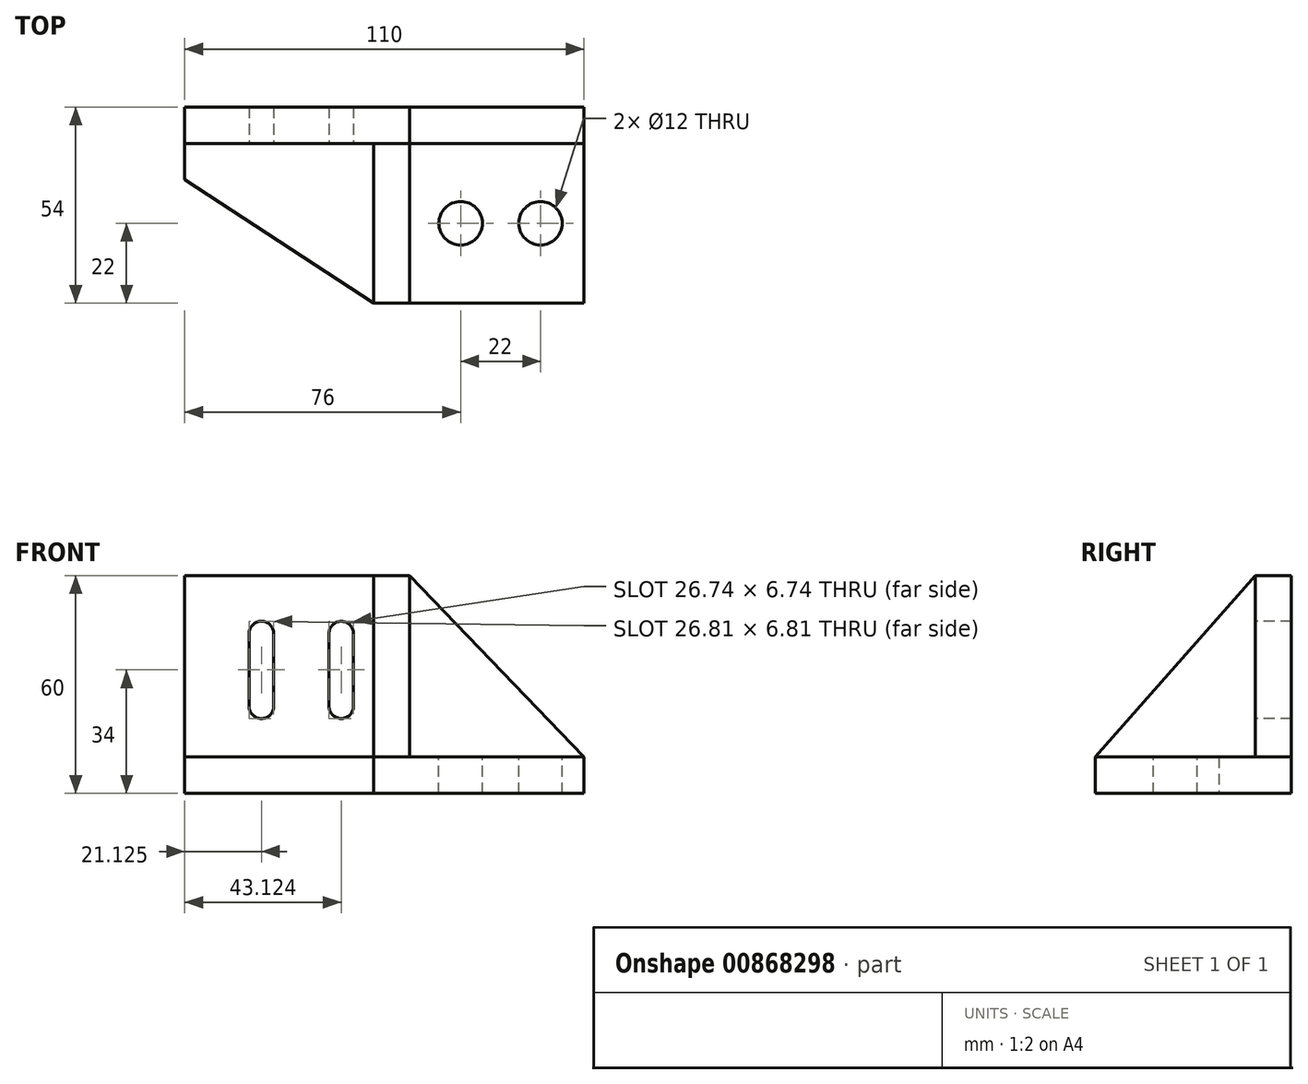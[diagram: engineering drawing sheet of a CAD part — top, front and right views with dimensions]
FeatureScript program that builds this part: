
annotation { "Feature Type Name" : "Feature", "Feature Type Description" : "" }
export const myFeature = defineFeature(function(context is Context, id is Id, definition is map)
    precondition{}
    {
        {
            var Q0;
            Q0=qCreatedBy(makeId("Top.planeOp"),FACE);
            var sketch = newSketch(context, id + "F0", { "sketchPlane" : qUnion([Q0])});
            skLineSegment(sketch, "E0.bottom", {"start": v(29, 27) * mm, "end": v(-29, 27) * mm});
            skLineSegment(sketch, "E0.top", {"start": v(29, -27) * mm, "end": v(-29, -27) * mm});
            skLineSegment(sketch, "E0.left", {"start": v(29, 27) * mm, "end": v(29, -27) * mm});
            skLineSegment(sketch, "E0.right", {"start": v(-29, 27) * mm, "end": v(-29, -27) * mm});
            skPoint(sketch, "E0.middle", {"position": v(0, 0) * mm});
            skLineSegment(sketch, "E1", {"start": v(-29, 27) * mm, "end": v(-81, 27) * mm});
            skLineSegment(sketch, "E2", {"start": v(-81, 27) * mm, "end": v(-81, 7) * mm});
            skLineSegment(sketch, "E3", {"start": v(-29, -27) * mm, "end": v(-81, 7) * mm});
            skSolve(sketch);
        }
        {
            var Q0;
            Q0=makeQuery(id+"F0.imprint","IMPRINT",FACE,{"disambiguationData":[TD([[makeQuery(id+"F0.imprint","IMPRINT",EDGE,{"derivedFrom":sQuery(id+"F0.wireOp",EDGE,"E0.bottom")}),1.0]])]});
            var Q1;
            Q1=makeQuery(id+"F0.imprint","IMPRINT",FACE,{"disambiguationData":[TD([[makeQuery(id+"F0.imprint","IMPRINT",EDGE,{"derivedFrom":sQuery(id+"F0.wireOp",EDGE,"E0.right")}),-1.0]])]});
            extrude(context, id + "F1", {"entities" : qUnion([Q0, Q1]), "depth" : 10 * mm, "offsetDistance" : 25 * mm});
        }
        {
            var Q0;
            Q0=makeQuery(id+"F1.opExtrude","SWEPT_FACE",FACE,{"disambiguationData":[OSD([sQuery(id+"F0.wireOp",EDGE,"E0.bottom")])]});
            var sketch = newSketch(context, id + "F2", { "sketchPlane" : qUnion([Q0])});
            skLineSegment(sketch, "E4", {"start": v(-29, 10) * mm, "end": v(19, 10) * mm});
            skLineSegment(sketch, "E5", {"start": v(19, 10) * mm, "end": v(19, 60) * mm});
            skLineSegment(sketch, "E6", {"start": v(19, 60) * mm, "end": v(-29, 10) * mm});
            skSolve(sketch);
        }
        {
            var Q0;
            Q0=makeQuery(id+"F2.imprint","IMPRINT",FACE,{"disambiguationData":[TD([[makeQuery(id+"F2.imprint","IMPRINT",EDGE,{"derivedFrom":sQuery(id+"F2.wireOp",EDGE,"E4")}),1.0]])]});
            extrude(context, id + "F3", {"entities" : qUnion([Q0]), "operationType" : NewBodyOperationType.ADD, "oppositeDirection" : true, "depth" : 10 * mm, "offsetDistance" : 25 * mm});
        }
        {
            var Q0;
            Q0=makeQuery(id+"F1.opExtrude","CAP_FACE",FACE,{"disambiguationData":[OSD([sQuery(id+"F0.wireOp",EDGE,"E0.bottom"),sQuery(id+"F0.wireOp",EDGE,"E0.top"),sQuery(id+"F0.wireOp",EDGE,"E0.left"),sQuery(id+"F0.wireOp",EDGE,"E1"),sQuery(id+"F0.wireOp",EDGE,"E2"),sQuery(id+"F0.wireOp",EDGE,"E3")])],"isStart":false});
            var sketch = newSketch(context, id + "F4", { "sketchPlane" : qUnion([Q0])});
            skLineSegment(sketch, "E7", {"start": v(-81, 17) * mm, "end": v(-19, 17) * mm});
            skLineSegment(sketch, "E8", {"start": v(-29, -27) * mm, "end": v(-29, 17) * mm});
            skLineSegment(sketch, "E9", {"start": v(-19, 17) * mm, "end": v(-19, -27) * mm});
            skCircle(sketch, "E10", {"center": v(17, -5) * mm, "radius": 6 * mm});
            skCircle(sketch, "E11", {"center": v(-5, -5) * mm, "radius": 6 * mm});
            skSolve(sketch);
        }
        {
            var Q0;
            {var subQ0=sQuery(id+"F4.wireOp",EDGE,"E7");Q0=makeQuery(id+"F4.imprint","IMPRINT",FACE,{"disambiguationData":[TD([[makeQuery(id+"F4.imprint","IMPRINT",EDGE,{"derivedFrom":subQ0}),1.0]])]});}
            extrude(context, id + "F5", {"entities" : qUnion([Q0]), "operationType" : NewBodyOperationType.ADD, "depth" : 50 * mm, "offsetDistance" : 25 * mm});
        }
        {
            var Q0;
            Q0=makeQuery(id+"F5.boolean.opBoolean","MERGE",FACE,{"derivedFrom":[makeQuery(id+"F3.opExtrude","CAP_FACE",FACE,{"disambiguationData":[OSD([sQuery(id+"F2.wireOp",EDGE,"E4"),sQuery(id+"F2.wireOp",EDGE,"E5"),sQuery(id+"F2.wireOp",EDGE,"E6")])],"isStart":false}),makeQuery(id+"F5.opExtrude","SWEPT_FACE",FACE,{"disambiguationData":[OSD([sQuery(id+"F4.wireOp",EDGE,"E7")])]})]});
            var sketch = newSketch(context, id + "F6", { "sketchPlane" : qUnion([Q0])});
            skLineSegment(sketch, "E12", {"start": v(-63.28, 44) * mm, "end": v(-63.28, 24) * mm});
            skLineSegment(sketch, "E13", {"start": v(-56.47, 44) * mm, "end": v(-56.47, 24) * mm});
            skLineSegment(sketch, "E14", {"start": v(-41.25, 44) * mm, "end": v(-41.25, 24) * mm});
            skLineSegment(sketch, "E15", {"start": v(-34.5, 44) * mm, "end": v(-34.5, 24) * mm});
            skArc(sketch, "E16", {"start": v(-63.28, 44) * mm, "mid": v(-59.88, 47.4) * mm, "end": v(-56.47, 44) * mm});
            skArc(sketch, "E17", {"start": v(-63.28, 24) * mm, "mid": v(-59.88, 20.6) * mm, "end": v(-56.47, 24) * mm});
            skArc(sketch, "E18", {"start": v(-41.25, 24) * mm, "mid": v(-37.88, 20.63) * mm, "end": v(-34.5, 24) * mm});
            skArc(sketch, "E19", {"start": v(-34.5, 44) * mm, "mid": v(-37.88, 47.37) * mm, "end": v(-41.25, 44) * mm});
            skSolve(sketch);
        }
        {
            var Q0;
            Q0 = qSketchRegion(id + "F4", true);
            var Q1;
            {var subQ3=sQuery(id+"F4.wireOp",EDGE,"E8");Q1=makeQuery(id+"F4.imprint","IMPRINT",FACE,{"disambiguationData":[TD([[makeQuery(id+"F4.imprint","IMPRINT",EDGE,{"derivedFrom":subQ3}),-1.0]])]});}
            extrude(context, id + "F7", {"entities" : qUnion([Q0, Q1]), "operationType" : NewBodyOperationType.ADD, "depth" : 50 * mm, "offsetDistance" : 25 * mm});
        }
        {
            var Q0;
            Q0=makeQuery(id+"F7.opExtrude","SWEPT_FACE",FACE,{"disambiguationData":[OSD([sQuery(id+"F4.wireOp",EDGE,"E9")])]});
            var sketch = newSketch(context, id + "F8", { "sketchPlane" : qUnion([Q0])});
            skLineSegment(sketch, "E20", {"start": v(-27, 10) * mm, "end": v(17, 60) * mm});
            skSolve(sketch);
        }
        {
            var Q0;
            Q0=makeQuery(id+"F8.imprint","IMPRINT",FACE,{"disambiguationData":[TD([[makeQuery(id+"F8.imprint","IMPRINT",EDGE,{"derivedFrom":sQuery(id+"F8.wireOp",EDGE,"E20")}),1.0]])]});
            extrude(context, id + "F9", {"entities" : qUnion([Q0]), "operationType" : NewBodyOperationType.REMOVE, "endBound" : BoundingType.THROUGH_ALL, "oppositeDirection" : true, "depth" : 25 * mm, "offsetDistance" : 25 * mm});
        }
        {
            var Q0;
            Q0=makeQuery(id+"F7.opExtrude","CAP_FACE",FACE,{"disambiguationData":[OSD([sQuery(id+"F4.wireOp",EDGE,"E11")])],"isStart":false});
            var Q1;
            Q1=makeQuery(id+"F7.opExtrude","CAP_FACE",FACE,{"disambiguationData":[OSD([sQuery(id+"F4.wireOp",EDGE,"E10")])],"isStart":false});
            extrude(context, id + "F10", {"entities" : qUnion([Q0, Q1]), "operationType" : NewBodyOperationType.REMOVE, "endBound" : BoundingType.THROUGH_ALL, "oppositeDirection" : true, "depth" : 25 * mm, "offsetDistance" : 25 * mm});
        }
        {
            var Q0;
            Q0=makeQuery(id+"F6.imprint","IMPRINT",FACE,{"disambiguationData":[TD([[makeQuery(id+"F6.imprint","IMPRINT",EDGE,{"derivedFrom":sQuery(id+"F6.wireOp",EDGE,"E12")}),1.0]])]});
            var Q1;
            Q1=makeQuery(id+"F6.imprint","IMPRINT",FACE,{"disambiguationData":[TD([[makeQuery(id+"F6.imprint","IMPRINT",EDGE,{"derivedFrom":sQuery(id+"F6.wireOp",EDGE,"E14")}),1.0]])]});
            extrude(context, id + "F11", {"entities" : qUnion([Q0, Q1]), "operationType" : NewBodyOperationType.REMOVE, "endBound" : BoundingType.THROUGH_ALL, "oppositeDirection" : true, "depth" : 25 * mm, "offsetDistance" : 25 * mm});
        }
    });
